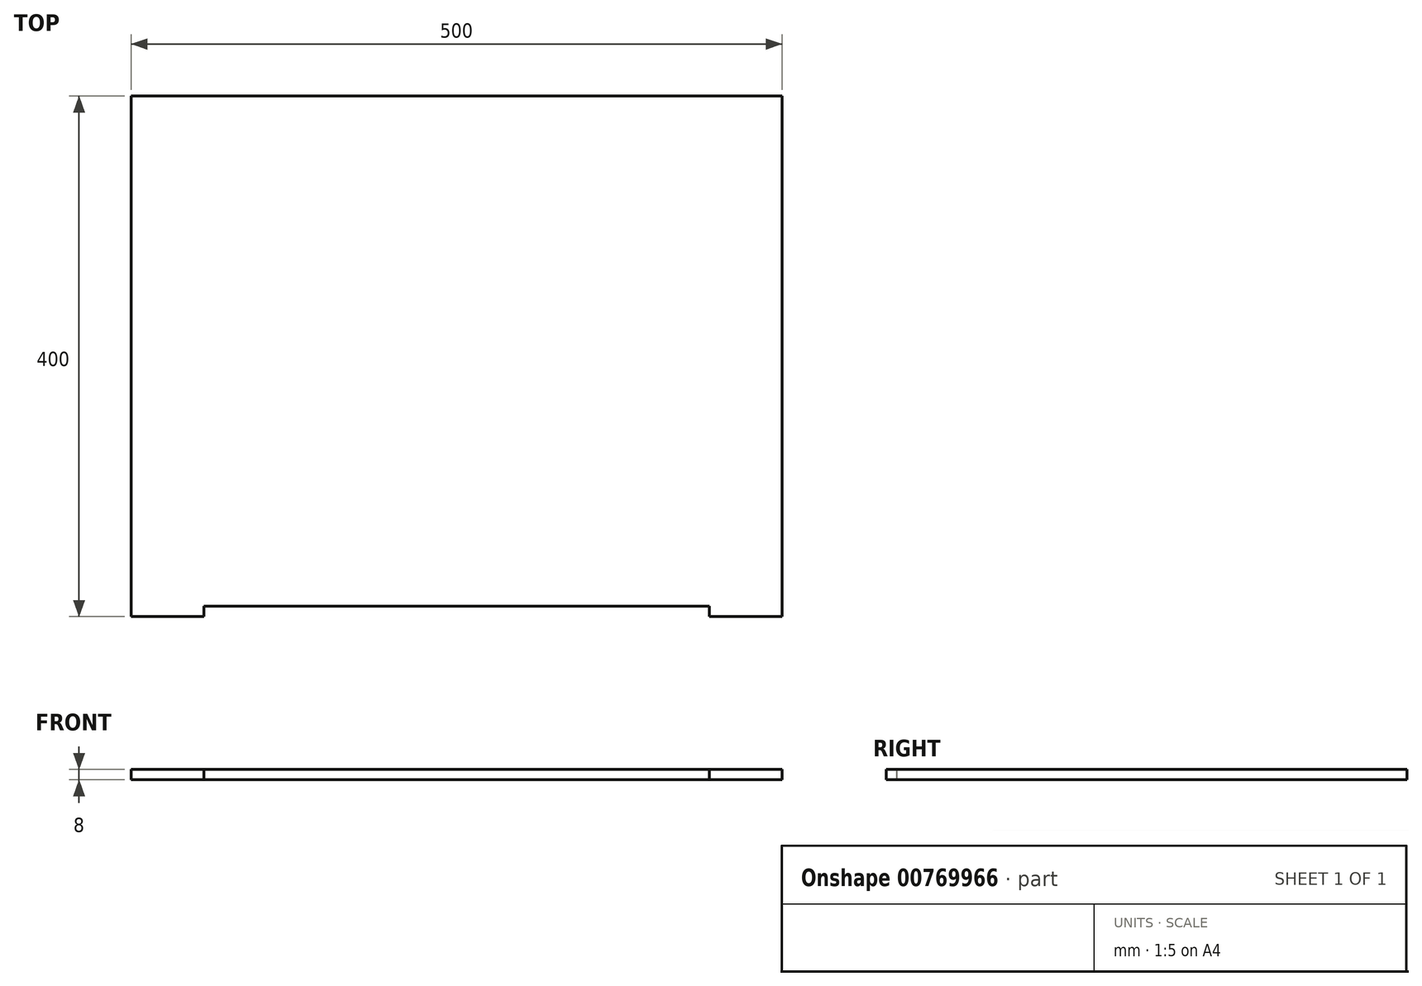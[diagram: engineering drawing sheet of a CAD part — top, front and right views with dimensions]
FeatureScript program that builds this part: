
annotation { "Feature Type Name" : "Feature", "Feature Type Description" : "" }
export const myFeature = defineFeature(function(context is Context, id is Id, definition is map)
    precondition{}
    {
        {
            var Q0;
            Q0=qCreatedBy(makeId("Top.planeOp"),FACE);
            var sketch = newSketch(context, id + "F0", { "sketchPlane" : qUnion([Q0])});
            skLineSegment(sketch, "E0.top", {"start": v(250, 200) * mm, "end": v(-250, 200) * mm});
            skLineSegment(sketch, "E0.left", {"start": v(250, -200) * mm, "end": v(250, 200) * mm});
            skLineSegment(sketch, "E0.right", {"start": v(-250, -200) * mm, "end": v(-250, 200) * mm});
            skPoint(sketch, "E0.middle", {"position": v(0, 0) * mm});
            skLineSegment(sketch, "E1", {"start": v(-250, -200) * mm, "end": v(-194, -200) * mm});
            skLineSegment(sketch, "E2", {"start": v(250, -200) * mm, "end": v(194, -200) * mm});
            skLineSegment(sketch, "E3", {"start": v(-194, -200) * mm, "end": v(-194, -192) * mm});
            skLineSegment(sketch, "E4", {"start": v(194, -200) * mm, "end": v(194, -192) * mm});
            skLineSegment(sketch, "E5", {"start": v(194, -192) * mm, "end": v(-194, -192) * mm});
            skSolve(sketch);
        }
        {
            var Q0;
            Q0=makeQuery(id+"F0.imprint","IMPRINT",FACE,{"disambiguationData":[TD([[makeQuery(id+"F0.imprint","IMPRINT",EDGE,{"derivedFrom":sQuery(id+"F0.wireOp",EDGE,"E0.bottom")}),-1.0]])]});
            var Q1;
            Q1=makeQuery(id+"F0.imprint","IMPRINT",FACE,{"disambiguationData":[TD([[makeQuery(id+"F0.imprint","IMPRINT",EDGE,{"derivedFrom":sQuery(id+"F0.wireOp",EDGE,"E0.top")}),1.0]])]});
            extrude(context, id + "F1", {"entities" : qUnion([Q0, Q1]), "depth" : 8 * mm, "offsetDistance" : 25 * mm});
        }
    });
